# Revit family: Urinal-Willoughby-1800-UW-BS
name_source: partatom
category: Plumbing Fixtures
revit_build: Autodesk Revit 2014 (Build: 20130308_1515(x64)
units: mm (PartAtom-declared; Revit-internal decimal feet)

## types (5) — shared parameters
CW Connection = No
Default Elevation = 0' - 0"
Fixture Body = Stainless Steel AISI 304-Willoughby
Flush Inlet Connection = Yes
HW Connection = No
Manufacturer = Willoughby Industries
Revision = A
URL = www.willoughby-ind.com
Vent Connection = No
Waste Connection = Yes
Waste DIA = 2"

## per-type parameters (varying)
| type | 36 inch | 48 inch | 60 inch | 72 inch | 96 inch | Description | Flush Inlet DIA | Model | Width | half width |
| 1872 | No | Yes | No | Yes | No | 72" Trough Urinal | 2" | UW-1872-BS | 6' - 0" | 3' - 0" |
| 1896 | No | No | No | No | Yes | 96" Trough Urinal | 2" | UW-1896-BS | 8' - 0" | 4' - 0" |
| 1860 | No | No | Yes | No | No | 60" Trough Urinal | 1" | UW-1860-BS | 5' - 0" | 2' - 6" |
| 1848 | No | Yes | No | No | No | 48" Trough Urinal | 1" | UW-1896-BS | 4' - 0" | 2' - 0" |
| 1836 | Yes | No | No | No | No | 36" Trough Urinal | 1" | UW-1896-BS | 3' - 0" | 1' - 6" |

## geometry (parser evidence)
native form markers: Sweep x1
no freeform markers — native parametric forms only
